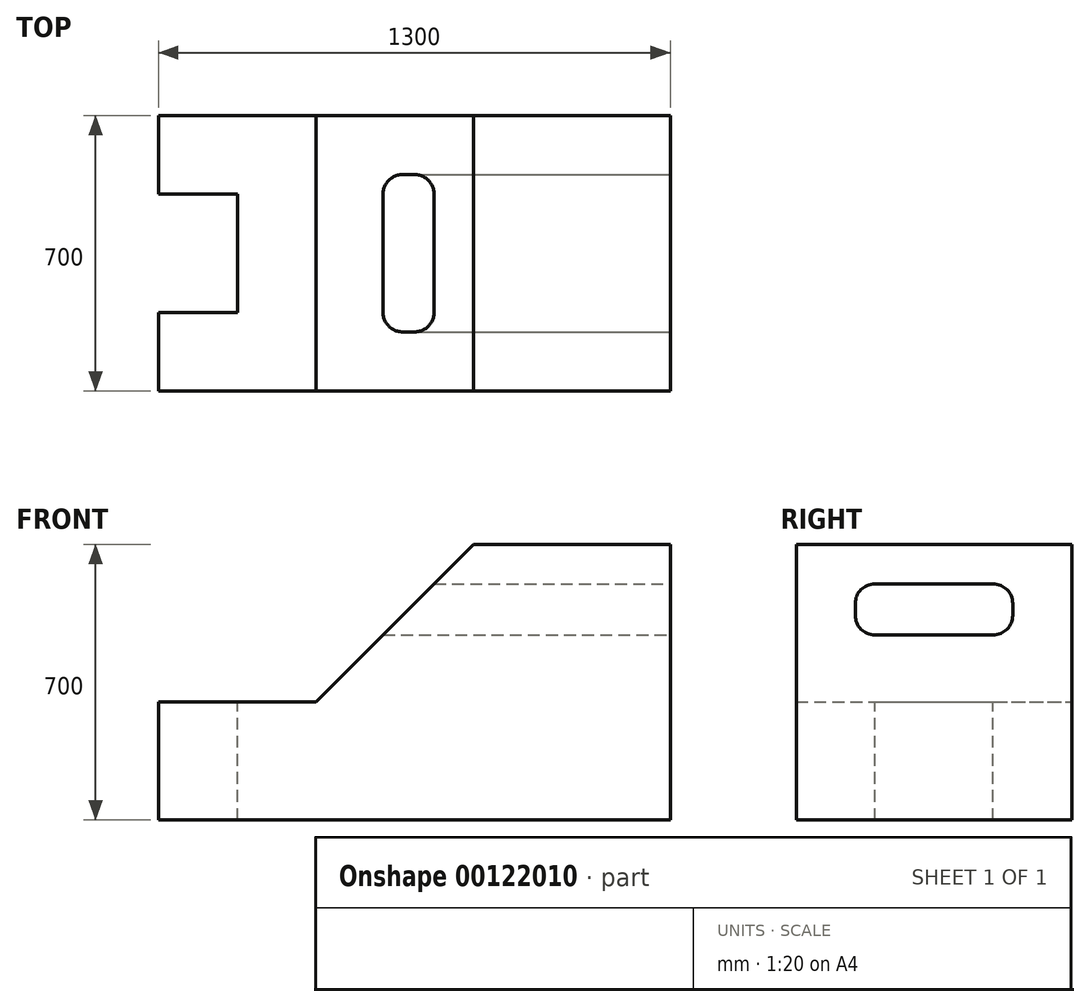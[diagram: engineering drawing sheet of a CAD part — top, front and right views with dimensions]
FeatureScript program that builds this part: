
annotation { "Feature Type Name" : "Feature", "Feature Type Description" : "" }
export const myFeature = defineFeature(function(context is Context, id is Id, definition is map)
    precondition{}
    {
        {
            var Q0;
            Q0=qCreatedBy(makeId("Front.planeOp"),FACE);
            var sketch = newSketch(context, id + "F0", { "sketchPlane" : qUnion([Q0])});
            skLineSegment(sketch, "E0.bottom", {"start": v(650, 350) * mm, "end": v(150, 350) * mm});
            skLineSegment(sketch, "E0.top", {"start": v(650, -350) * mm, "end": v(-650, -350) * mm});
            skLineSegment(sketch, "E0.left", {"start": v(650, 350) * mm, "end": v(650, -350) * mm});
            skLineSegment(sketch, "E0.right", {"start": v(-650, -50) * mm, "end": v(-650, -350) * mm});
            skPoint(sketch, "E0.middle", {"position": v(0, 0) * mm});
            skLineSegment(sketch, "E1", {"start": v(150, 350) * mm, "end": v(-250, -50) * mm});
            skLineSegment(sketch, "E2", {"start": v(-250, -50) * mm, "end": v(-650, -50) * mm});
            skPoint(sketch, "E3.orphan", {"position": v(-650, 350) * mm});
            skSolve(sketch);
        }
        {
            var Q0;
            Q0=makeQuery(id+"F0.imprint","IMPRINT",FACE,{"disambiguationData":[TD([[makeQuery(id+"F0.imprint","IMPRINT",EDGE,{"derivedFrom":sQuery(id+"F0.wireOp",EDGE,"E0.top")}),-1.0]])]});
            extrude(context, id + "F1", {"entities" : qUnion([Q0]), "depth" : 700 * mm});
        }
        {
            var Q0;
            Q0=makeQuery(id+"F1.opExtrude","SWEPT_FACE",FACE,{"disambiguationData":[OSD([sQuery(id+"F0.wireOp",EDGE,"E0.left")])]});
            var sketch = newSketch(context, id + "F2", { "sketchPlane" : qUnion([Q0])});
            skLineSegment(sketch, "E4.bottom", {"start": v(-500, 120.14) * mm, "end": v(-200, 120.14) * mm});
            skLineSegment(sketch, "E4.top", {"start": v(-500, 250) * mm, "end": v(-200, 250) * mm});
            skLineSegment(sketch, "E4.left", {"start": v(-550, 170.14) * mm, "end": v(-550, 200) * mm});
            skLineSegment(sketch, "E4.right", {"start": v(-150, 170.14) * mm, "end": v(-150, 200) * mm});
            skPoint(sketch, "E4.middle", {"position": v(-350, 185.07) * mm});
            skPoint(sketch, "E5.visualSharp", {"position": v(-550, 250) * mm});
            skArc(sketch, "E5.filletArc", {"start": v(-500, 250) * mm, "mid": v(-535.36, 235.36) * mm, "end": v(-550, 200) * mm});
            skPoint(sketch, "E6.visualSharp", {"position": v(-550, 120.14) * mm});
            skArc(sketch, "E6.filletArc", {"start": v(-550, 170.14) * mm, "mid": v(-535.36, 134.79) * mm, "end": v(-500, 120.14) * mm});
            skPoint(sketch, "E7.visualSharp", {"position": v(-150, 250) * mm});
            skArc(sketch, "E7.filletArc", {"start": v(-150, 200) * mm, "mid": v(-164.64, 235.36) * mm, "end": v(-200, 250) * mm});
            skPoint(sketch, "E8.visualSharp", {"position": v(-150, 120.14) * mm});
            skArc(sketch, "E8.filletArc", {"start": v(-200, 120.14) * mm, "mid": v(-164.64, 134.79) * mm, "end": v(-150, 170.14) * mm});
            skSolve(sketch);
        }
        {
            var Q0;
            Q0 = qSketchRegion(id + "F2", true);
            extrude(context, id + "F3", {"entities" : qUnion([Q0]), "operationType" : NewBodyOperationType.REMOVE, "endBound" : BoundingType.THROUGH_ALL, "oppositeDirection" : true, "depth" : 25.4 * mm});
        }
        {
            var Q0;
            Q0=makeQuery(id+"F1.opExtrude","SWEPT_FACE",FACE,{"disambiguationData":[OSD([sQuery(id+"F0.wireOp",EDGE,"E2")])]});
            var sketch = newSketch(context, id + "F4", { "sketchPlane" : qUnion([Q0])});
            skLineSegment(sketch, "E9.bottom", {"start": v(-450, -500) * mm, "end": v(-650, -500) * mm});
            skLineSegment(sketch, "E9.top", {"start": v(-450, -200) * mm, "end": v(-650, -200) * mm});
            skLineSegment(sketch, "E9.left", {"start": v(-450, -500) * mm, "end": v(-450, -200) * mm});
            skPoint(sketch, "E9.middle", {"position": v(-650, -350) * mm});
            skPoint(sketch, "E10.orphan", {"position": v(-850, -200) * mm});
            skPoint(sketch, "E11.orphan", {"position": v(-850, -500) * mm});
            skLineSegment(sketch, "E12", {"start": v(-650, -200) * mm, "end": v(-650, -500) * mm});
            skSolve(sketch);
        }
        {
            var Q0;
            Q0 = qSketchRegion(id + "F4", true);
            extrude(context, id + "F5", {"entities" : qUnion([Q0]), "operationType" : NewBodyOperationType.REMOVE, "endBound" : BoundingType.THROUGH_ALL, "oppositeDirection" : true, "depth" : 25.4 * mm});
        }
    });
